# Revit family: rba-bim-b369039
name_source: partatom
category: Specialty Equipment
revit_build: Autodesk Revit 2015 (Build: 20140223_1515(x64)
units: mm (PartAtom-declared; Revit-internal decimal feet)

## types (1)
- B-369039
    Assembly Code = E1090900
    Capacity = 300 C-fold Towels  ;  400 Multifold Towels  ;  1.6 gal Waste
    Default Elevation = 1219 mm
    Description = Bobrick B-36903 TrimLine Series Surface Mounted Combination Towel and Waste Unit
    Expected Lifespan (Years) = 0
    Finish Material = Stainless Steel - Bobrick - Satin
    Keynote = 102813
    Maintenance Schedule (Months) = 0
    Manufacturer = Bobrick Washroom Equipment, Inc.
    Manufacturer Website = http://www.bobrick.com
    Model = B-369039
    Modified Issue = 20160816.01
    Recess Into Host = 92 mm
    URL = http://www.rba.com.au
    Unit Depth = 106 mm
    Unit Height = 791 mm
    Unit Width = 330 mm
    Warranty Duration (Years) = 0

## geometry (parser evidence)
native form markers: Blend x6, Sweep x8
no freeform markers — native parametric forms only
